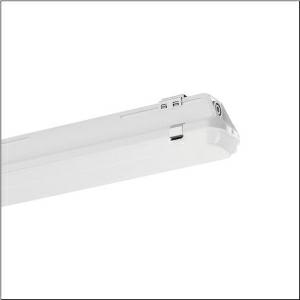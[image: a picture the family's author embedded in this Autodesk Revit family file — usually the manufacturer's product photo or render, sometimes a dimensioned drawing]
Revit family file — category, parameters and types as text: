
# Revit family: monsun_r__21_51fb107p440k_2386
name_source: partatom
category: Lighting Fixtures
units: mm (PartAtom-declared; Revit-internal decimal feet)

## family parameters
Cut with Voids When Loaded = No
Host = Face
Light Source = No
Part Type = Normal
Room Calculation Point = No
Round Connector Dimension = Use Diameter
Shared = No

## types (1)
- Monsun® 21 (1 x LED, 4400 lm, 24.8 W, 4000K)
    Apparent Load = 25 VA
    CIE Flux Codes = 47 77 93 94 100
    Color Rendering = 80
    Color Temperature = 4000K
    Default Elevation = 1800 mm
    Description = Monsun® 21, damp-proof luminaire, chain hanger, primary optical cover: enclosure, of PMMA, light emission: direct distribution, primary light characteristic: symmetric, installation type: suspended mounting, surface-mounted, horizontal mounting, vertical mounting, LED, rated luminous flux: 4.400lm, luminous efficacy: 177lm/W, light colour: 840, colour temperature: 4000K, control gear: ON/OFF, with terminal, 3-pole, max. 2.5mm², mains connection: 220..240V, AC, 50/60Hz, rated input power: 25W, housing, of glass-fibre reinforced polyester, uncoated, bright grey, incl. chain hanger, length: 1.590mm, width: 90mm, height: 88mm, clip for enclosure, of stainless steel (V2A), ceiling mounting element, of stainless steel (V2A), chain hanger, of stainless steel (V2A), protection rating (complete): IP66, insulation class (complete): insulation class I (protective earthing), certification: CE, ENEC, VDE, UKCA, protection symbol: D, impact resistance: IK04, permissible operating ambient temperature: -25..+35°C, standard: EN 50419, EN 60598-2-1, corresponds to IFS (International Featured Standards) requirements for safety and quality in the food industry, for indoor or canopied outdoor use, no direct snow, no direct sun, no direct rain, LABS conformity tested according to VDMA 24364:2018-05, contact your sales advisor before using the luminaires in applications with unclear chemical exposure, large temperature fluctuations or condensation-forming humidity, packaging unit: 1 piece
    Height = 89 mm
    Lamp = 1 x LED
    Lamp Light Flux = 4400 lm
    Lamp Power = 24.8 W
    Lamp count = 1
    Length = 1590 mm
    Luminous efficacy = 177 lm/W
    Manufacturer = Siteco
    ModVariant = No
    Model = 51FB107P440K
    Mounting Place = Ceiling
    Mounting Type = Surface mounted
    Number of Poles = 1
    OnlyDefault = Yes
    Power Factor = 1
    Product Name = Monsun® 21
    Product group = damp-proof luminaire
    ProductGroupID = 300
    Protection Class = Protection class I
    Protection Degree = IP 66
    RLX_Detail_Level = 1
    RLX_Emergency_Light_Flux = 0 lm
    RLX_Emergency_Type = 0
    RLX_Emergency_Type_DB = No
    RlxData = <blob elided: 88341 chars, md5=a1e5a463>
    Socket = socket
    Standby Power = 0 W
    System Light Flux = 4400 lm
    System Power = 25 W
    Type Comments = Product without accessories
    Type Image = l_1319656.jpg
    URL = http://relux.com
    VarID = ---
    Voltage = 0 V
    Weight = 0.00 kg
    Width = 90 mm

## geometry (parser evidence)
native form markers: Blend x4, Sweep x15
no freeform markers — native parametric forms only
